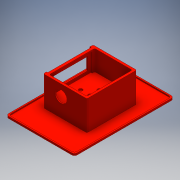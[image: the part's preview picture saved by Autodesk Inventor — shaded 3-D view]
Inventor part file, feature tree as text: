
AUTODESK INVENTOR PART (.ipt)
format: ipt  version: 2016 (Build 200138000, 138)  size: 261,120 bytes
history: native  units: mm
features: extrude x10, sketch x9
ambient origin geometry x8: Origin, YZ Plane, XZ Plane, XY Plane, X Axis, Y Axis, Z Axis, Center Point
bodies: Solid1 (feature_tree)
feature tree (19):
  extrude  "xyAttach"  Depth=159.75mm
  extrude  "chamberExtrusion"  Depth=4.0mm
  extrude  "coverSlipMountExt"  Depth=3.0mm
  extrude  "coverSlipWindowExt"  Depth=80.0mm
  extrude  "illObjExt"  Depth=40.0mm
  extrude  "circCovSlipMount"  Depth=3.5mm
  extrude  "circCovSlipWindowExt"  Depth=6.0mm
  extrude  "chamberBaseInsert"  Depth=47.5mm TaperAngle=0.0deg
  extrude  "magnetsExtrusion"  Depth=2.0mm
  extrude  "Extrusion11"  Depth=2.0mm
  sketch  "Sketch1"  dims[d0=159.75mm d1=79.875mm]
  sketch  "Sketch2"  dims[d2=109.75mm d3=4.0mm]
  sketch  "Sketch5"  dims[d4=3.0mm d5=0.0mm d6=54.875mm]
  sketch  "Sketch6"  dims[d7=70.0mm d8=80.0mm]
  sketch  "Sketch7"  dims[d9=40.0mm d10=35.0mm]
  sketch  "Sketch8"  dims[d11=3.5mm d12=3.5mm]
  sketch  "Sketch9"  dims[d13=3.5mm d14=6.0mm]
  sketch  "Sketch10"  dims[d15=2.0mm d16=47.5mm d17=0.0mm]
  sketch  "Sketch12"  dims[d18=5.65mm d19=5.65mm d20=5.65mm d21=5.65mm d22=5.65mm d23=15.0mm d24=15.0mm d25=15.0mm d26=15.0mm d27=2.75mm d28=0.0mm d29=65.0mm d30=30.0mm d31=32.5mm d32=45.0mm d33=2.0mm d34=0.0mm d35=55.0mm d36=20.0mm d37=27.5mm d38=40.0mm d39=2.0mm d40=0.0mm d41=70.0mm d42=35.0mm d43=2.0mm d44=0.0mm d45=25.0mm d48=2.0mm d49=0.0mm d50=19.0mm d51=2.0mm d52=0.0mm d53=26.5mm d56=30.0mm d57=2.0mm d58=15.0mm d59=0.0mm d67=4.0mm d68=2.0mm d69=2.0mm d70=2.0mm d71=2.0mm d72=2.0mm d73=0.0mm]
